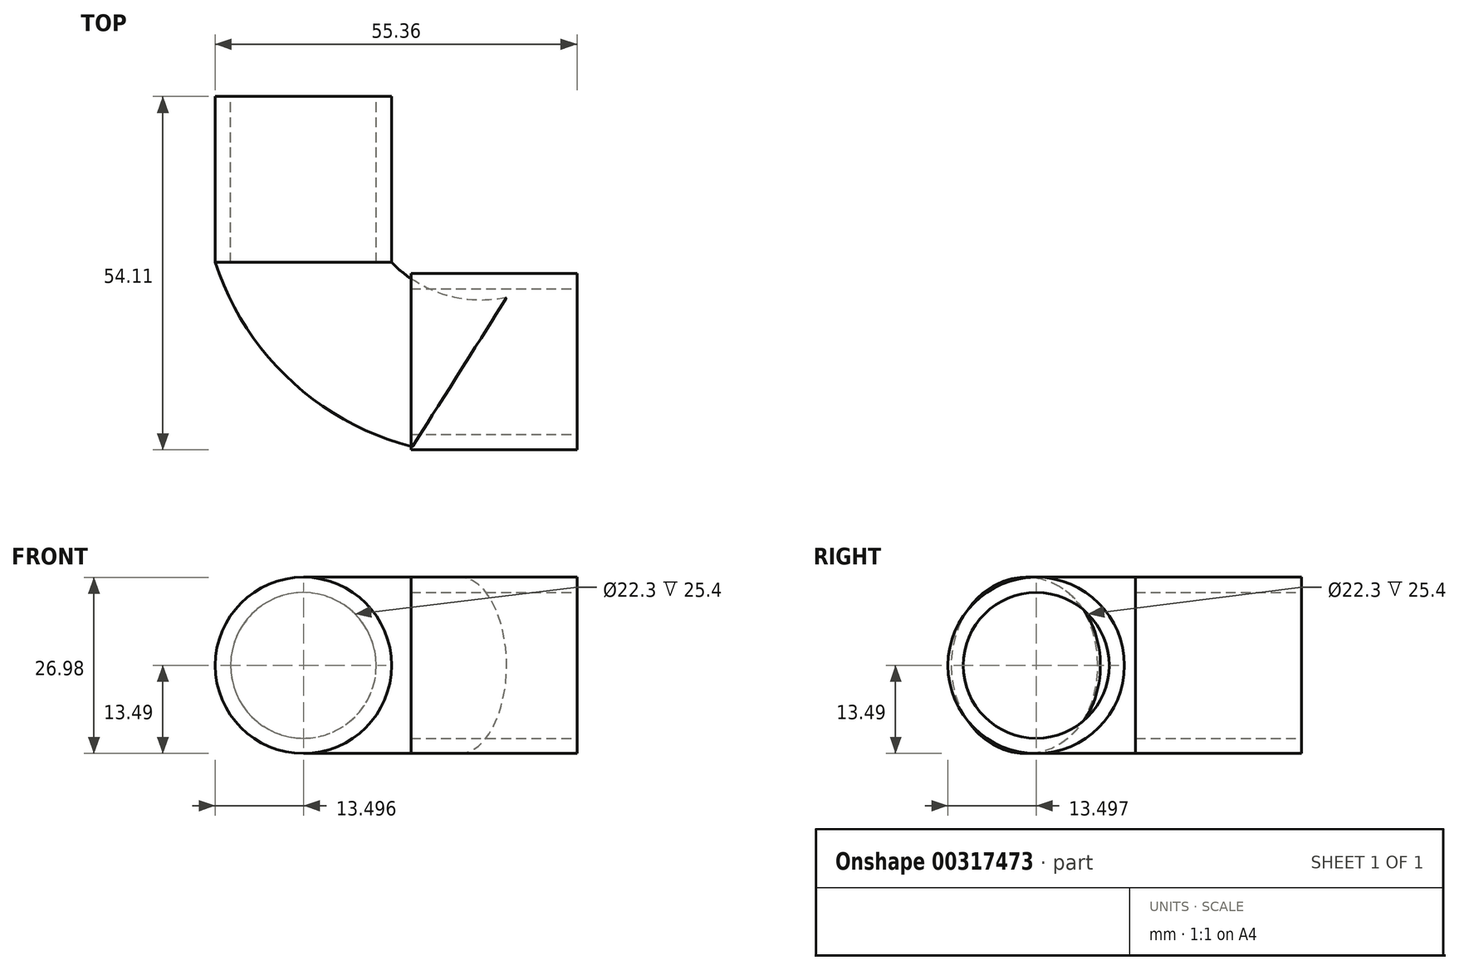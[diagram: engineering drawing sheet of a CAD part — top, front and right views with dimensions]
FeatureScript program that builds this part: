
annotation { "Feature Type Name" : "Feature", "Feature Type Description" : "" }
export const myFeature = defineFeature(function(context is Context, id is Id, definition is map)
    precondition{}
    {
        {
            var Q0;
            Q0=qCreatedBy(makeId("Right.planeOp"),FACE);
            var sketch = newSketch(context, id + "F0", { "sketchPlane" : qUnion([Q0])});
            skCircle(sketch, "E0", {"center": v(-15.21, 0) * mm, "radius": 13.5 * mm});
            skPoint(sketch, "E0.first.point", {"position": v(-2.5, 4.55) * mm});
            skPoint(sketch, "E0.second.point", {"position": v(-28.6, 1.69) * mm});
            skPoint(sketch, "E0.third.point", {"position": v(-28.7, 0.48) * mm});
            skSolve(sketch);
        }
        {
            var Q0;
            Q0=makeQuery(id+"F0.imprint","IMPRINT",FACE,{"disambiguationData":[TD([[makeQuery(id+"F0.imprint","IMPRINT",EDGE,{"derivedFrom":sQuery(id+"F0.wireOp",EDGE,"E0")}),1.0]])]});
            extrude(context, id + "F1", {"entities" : qUnion([Q0]), "depth" : 25.4 * mm});
        }
        {
            var Q0;
            Q0=qCreatedBy(makeId("Front.planeOp"),FACE);
            var sketch = newSketch(context, id + "F2", { "sketchPlane" : qUnion([Q0])});
            skCircle(sketch, "E1", {"center": v(-16.46, 0) * mm, "radius": 13.5 * mm});
            skPoint(sketch, "E1.first.point", {"position": v(-18.9, -13.27) * mm});
            skPoint(sketch, "E1.second.point", {"position": v(-15.77, -13.48) * mm});
            skPoint(sketch, "E1.third.point", {"position": v(-20.9, -12.74) * mm});
            skPoint(sketch, "E2", {"position": v(-24.5, -10.84) * mm});
            skPoint(sketch, "E3", {"position": v(0, 0) * mm});
            skSolve(sketch);
        }
        {
            var Q0;
            Q0 = qSketchRegion(id + "F2", true);
            var Q1;
            Q1=qCreatedBy(makeId("Top.planeOp"),FACE);
            extrude(context, id + "F3", {"entities" : qUnion([Q0]), "oppositeDirection" : true, "endBoundEntityFace" : qUnion([Q1]), "depth" : 25.4 * mm});
        }
        {
            var Q0;
            Q0=makeQuery(id+"F3.opExtrude","CAP_FACE",FACE,{"disambiguationData":[OSD([sQuery(id+"F2.wireOp",EDGE,"E1")])],"isStart":true});
            var sketch = newSketch(context, id + "F4", { "sketchPlane" : qUnion([Q0])});
            skPoint(sketch, "E4", {"position": v(-17.05, 13.48) * mm});
            skSolve(sketch);
        }
        {
            var Q0;
            Q0=makeQuery(id+"F1.opExtrude","CAP_FACE",FACE,{"disambiguationData":[OSD([sQuery(id+"F0.wireOp",EDGE,"E0")])],"isStart":false});
            var sketch = newSketch(context, id + "F5", { "sketchPlane" : qUnion([Q0])});
            skCircle(sketch, "E5", {"center": v(-15.21, 0) * mm, "radius": 11.15 * mm});
            skSolve(sketch);
        }
        {
            var Q0;
            Q0=makeQuery(id+"F5.imprint","IMPRINT",FACE,{"disambiguationData":[TD([[makeQuery(id+"F5.imprint","IMPRINT",EDGE,{"derivedFrom":sQuery(id+"F5.wireOp",EDGE,"E5")}),1.0]])]});
            extrude(context, id + "F6", {"entities" : qUnion([Q0]), "operationType" : NewBodyOperationType.REMOVE, "oppositeDirection" : true, "depth" : 46.74 * mm});
        }
        {
            var Q0;
            Q0=makeQuery(id+"F3.opExtrude","CAP_FACE",FACE,{"disambiguationData":[OSD([sQuery(id+"F2.wireOp",EDGE,"E1")])],"isStart":false});
            var sketch = newSketch(context, id + "F7", { "sketchPlane" : qUnion([Q0])});
            skCircle(sketch, "E6", {"center": v(16.46, 0) * mm, "radius": 11.15 * mm});
            skSolve(sketch);
        }
        {
            var Q0;
            Q0 = qSketchRegion(id + "F7", true);
            extrude(context, id + "F8", {"entities" : qUnion([Q0]), "operationType" : NewBodyOperationType.REMOVE, "oppositeDirection" : true, "depth" : 50.8 * mm});
        }
        {
            var Q0;
            Q0=qCreatedBy(makeId("Top.planeOp"),FACE);
            var sketch = newSketch(context, id + "F9", { "sketchPlane" : qUnion([Q0])});
            skPoint(sketch, "E7", {"position": v(0, -28.56) * mm});
            skPoint(sketch, "E8", {"position": v(-30.36, 0) * mm});
            skArc(sketch, "E9", {"start": v(-30.36, 0) * mm, "mid": v(-18.86, -18.19) * mm, "end": v(0, -28.56) * mm});
            skSolve(sketch);
        }
        {
            var Q0;
            Q0=makeQuery(id+"F4.imprint","IMPRINT",FACE,{"disambiguationData":[TD([[makeQuery(id+"F4.imprint","IMPRINT",EDGE,{"derivedFrom":makeQuery(id+"F3.opExtrude","CAP_EDGE",EDGE,{"disambiguationData":[OSD([sQuery(id+"F2.wireOp",EDGE,"E1")])],"isStart":true})}),1.0]])]});
            var Q1;
            Q1=sQuery(id+"F9.wireOp",EDGE,"E9");
            sweep(context, id + "F10", {"profiles" : qUnion([Q0]), "path" : qUnion([Q1])});
        }
    });
